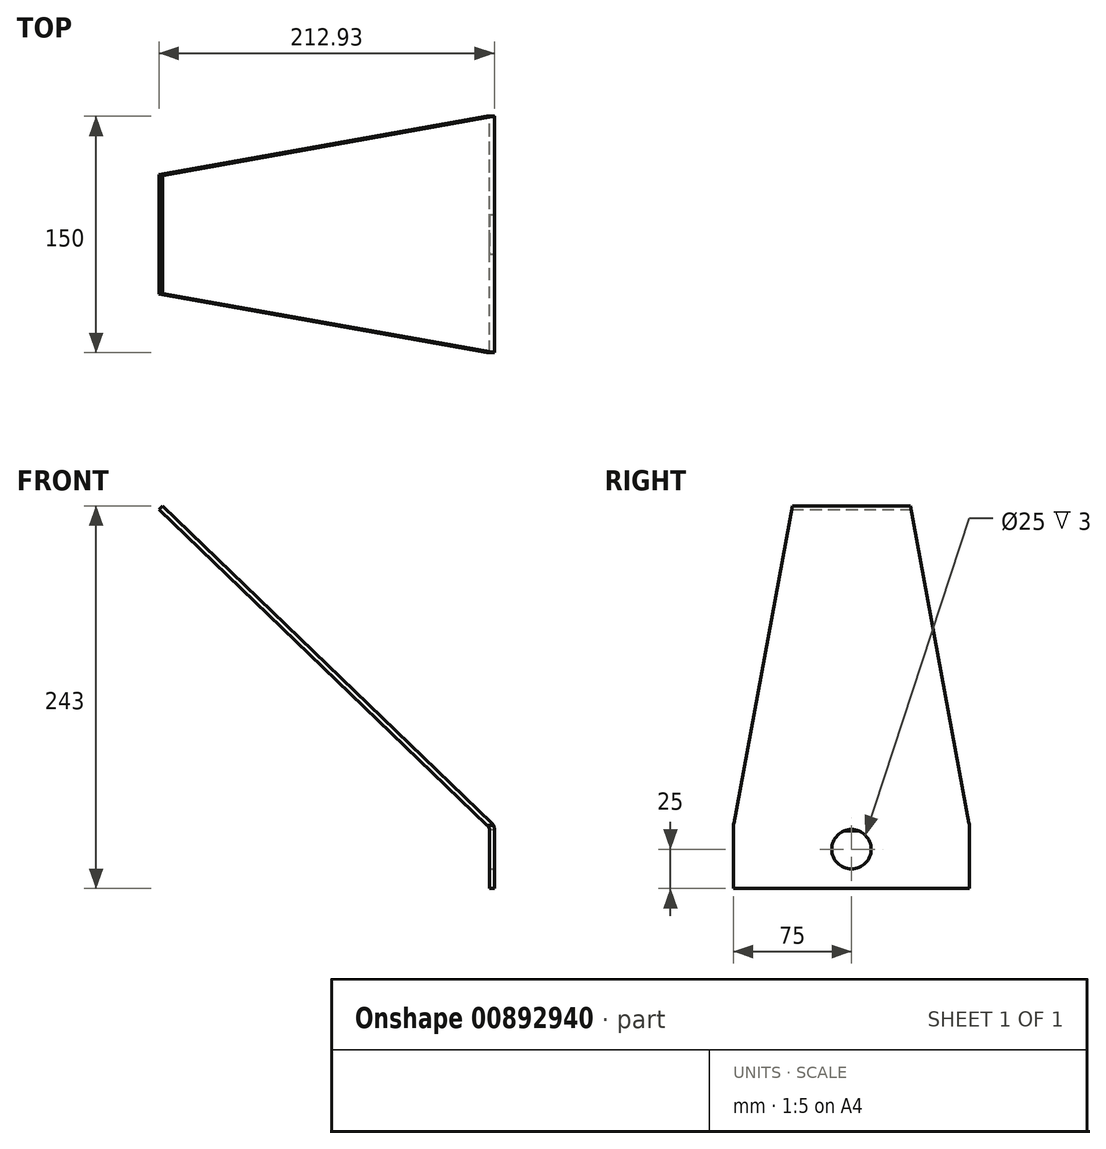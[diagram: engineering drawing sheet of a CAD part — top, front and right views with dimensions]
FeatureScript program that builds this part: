
annotation { "Feature Type Name" : "Feature", "Feature Type Description" : "" }
export const myFeature = defineFeature(function(context is Context, id is Id, definition is map)
    precondition{}
    {
        {
            var Q0;
            Q0=qCreatedBy(makeId("Front.planeOp"),FACE);
            var sketch = newSketch(context, id + "F0", { "sketchPlane" : qUnion([Q0])});
            skLineSegment(sketch, "E0", {"start": v(279.5, -25) * mm, "end": v(279.5, 13.72) * mm});
            skLineSegment(sketch, "E1", {"start": v(279.5, 13.72) * mm, "end": v(69.57, 215.84) * mm});
            skLineSegment(sketch, "E2", {"start": v(69.57, 215.84) * mm, "end": v(71.65, 218) * mm});
            skLineSegment(sketch, "E3", {"start": v(71.65, 218) * mm, "end": v(282.5, 15) * mm});
            skLineSegment(sketch, "E4", {"start": v(282.5, 15) * mm, "end": v(282.5, -25) * mm});
            skLineSegment(sketch, "E5", {"start": v(282.5, -25) * mm, "end": v(279.5, -25) * mm});
            skCircle(sketch, "E6", {"center": v(0, 230) * mm, "radius": 71 * mm, "construction": true});
            skSolve(sketch);
        }
        {
            var Q0;
            Q0 = qSketchRegion(id + "F0", true);
            extrude(context, id + "F1", {"entities" : qUnion([Q0]), "endBound" : BoundingType.SYMMETRIC, "depth" : (300 / 2) * mm, "offsetDistance" : 25 * mm});
        }
        {
            var Q0;
            Q0=makeQuery(id+"F1.opExtrude","SWEPT_EDGE",EDGE,{"disambiguationData":[OSD([sQuery(id+"F0.wireOp",EDGE,"E0"),sQuery(id+"F0.wireOp",EDGE,"E1")])]});
            var Q1;
            Q1=makeQuery(id+"F1.opExtrude","SWEPT_EDGE",EDGE,{"disambiguationData":[OSD([sQuery(id+"F0.wireOp",EDGE,"E3"),sQuery(id+"F0.wireOp",EDGE,"E4")])]});
            fillet(context, id + "F2", {"entities" : qUnion([Q0, Q1]), "radius" : 5 * mm, "tangentPropagation" : true, "allowEdgeOverflow" : false});
        }
        {
            var Q0;
            Q0=makeQuery(id+"F1.opExtrude","SWEPT_FACE",FACE,{"disambiguationData":[OSD([sQuery(id+"F0.wireOp",EDGE,"E4")])]});
            var sketch = newSketch(context, id + "F3", { "sketchPlane" : qUnion([Q0])});
            skCircle(sketch, "E7", {"center": v(0, 0) * mm, "radius": 12.5 * mm});
            skSolve(sketch);
        }
        {
            var Q0;
            Q0 = qSketchRegion(id + "F3", true);
            var Q1;
            Q1=makeQuery(id+"F1.opExtrude","SWEPT_FACE",FACE,{"disambiguationData":[OSD([sQuery(id+"F0.wireOp",EDGE,"E0")])]});
            extrude(context, id + "F4", {"entities" : qUnion([Q0]), "operationType" : NewBodyOperationType.REMOVE, "endBound" : BoundingType.UP_TO_SURFACE, "oppositeDirection" : true, "depth" : 25 * mm, "endBoundEntityFace" : qUnion([Q1]), "offsetDistance" : 25 * mm});
        }
        {
            var Q0;
            Q0=qCreatedBy(makeId("Right.planeOp"),FACE);
            var sketch = newSketch(context, id + "F5", { "sketchPlane" : qUnion([Q0])});
            skLineSegment(sketch, "E8", {"start": v(-75, -25) * mm, "end": v(-75, 15.2) * mm});
            skLineSegment(sketch, "E9", {"start": v(-75, 15.2) * mm, "end": v(-37.5, 218) * mm});
            skLineSegment(sketch, "E10", {"start": v(-37.5, 218) * mm, "end": v(0, 218) * mm});
            skLineSegment(sketch, "E11", {"start": v(0, -25) * mm, "end": v(-75, -25) * mm});
            skLineSegment(sketch, "E12", {"start": v(0, -49.14) * mm, "end": v(0, 260.15) * mm});
            skLineSegment(sketch, "E13.MirrorCS", {"start": v(75, 15.2) * mm, "end": v(37.5, 218) * mm});
            skLineSegment(sketch, "E14.MirrorCS", {"start": v(37.5, 218) * mm, "end": v(0, 218) * mm});
            skLineSegment(sketch, "E15.MirrorCS", {"start": v(0, -25) * mm, "end": v(75, -25) * mm});
            skLineSegment(sketch, "E16.MirrorCS", {"start": v(75, -25) * mm, "end": v(75, 15.2) * mm});
            skSolve(sketch);
        }
        {
            var Q0;
            Q0 = qSketchRegion(id + "F5", true);
            extrude(context, id + "F6", {"entities" : qUnion([Q0]), "operationType" : NewBodyOperationType.INTERSECT, "endBound" : BoundingType.THROUGH_ALL, "depth" : 25 * mm, "offsetDistance" : 25 * mm});
        }
    });
